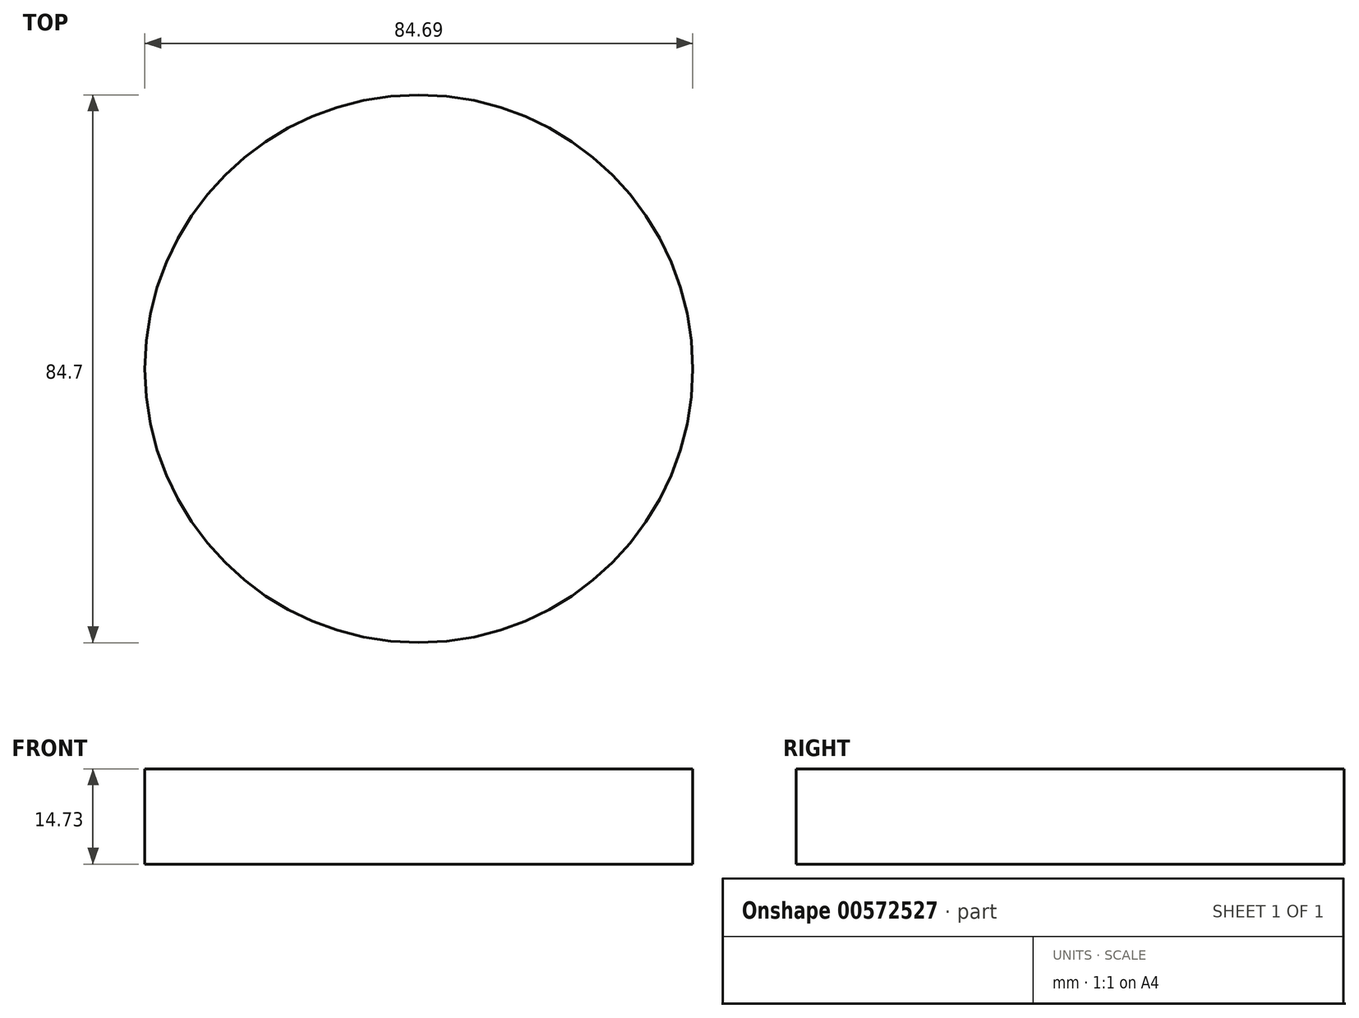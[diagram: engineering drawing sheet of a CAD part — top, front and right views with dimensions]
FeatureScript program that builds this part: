
annotation { "Feature Type Name" : "Feature", "Feature Type Description" : "" }
export const myFeature = defineFeature(function(context is Context, id is Id, definition is map)
    precondition{}
    {
        {
            var Q0;
            Q0=qCreatedBy(makeId("Top.planeOp"),FACE);
            var sketch = newSketch(context, id + "F0", { "sketchPlane" : qUnion([Q0])});
            skCircle(sketch, "E0", {"center": v(-19.78, 12.8) * mm, "radius": 42.35 * mm});
            skSolve(sketch);
        }
        {
            var Q0;
            Q0=makeQuery(id+"F0.imprint","IMPRINT",FACE,{"disambiguationData":[TD([[makeQuery(id+"F0.imprint","IMPRINT",EDGE,{"derivedFrom":sQuery(id+"F0.wireOp",EDGE,"E0")}),1.0]])]});
            extrude(context, id + "F1", {"entities" : qUnion([Q0]), "depth" : 14.73 * mm, "offsetDistance" : 25.4 * mm});
        }
    });
